# Revit family: Power-ModularDevices-GEWISS-90RCD-BDHP_4P
name_source: partatom
category: Apparecchi elettrici
revit_build: Autodesk Revit MEP 2016 (Build: 20150220_1215(x64)
units: mm (PartAtom-declared; Revit-internal decimal feet)

## family parameters
Condiviso = Sì
Host = Superficie
Mantenere orientamento annotazione = Sì
Numero OmniClass = 23.80.50.00
Punto di calcolo locali = Sì
Quota connettore circolare = Usa diametro
Taglio con vuoti quando caricato = No
Tipo di parte = Normale
Titolo OmniClass = Terminals for Power Supply

## types (1)
- Power-ModularDevices-GEWISS-90RCD-BDHP_4P
    Adjustable tripping time = 0 - 60 - 150 ms
    Assembly position: = Any
    Catalogue = POWER
    Catalogue Range = 90 RCD
    Description = HIGH PERFORMANCE  RESIDUAL CURRENT DEVICE
    Descrizione = HP ADD-ON RCD 4P In<125A ADJ.A 0.3/3 6M
    EAN code = 8011564126121
    Electrocod = 1412
    IDF = 33a27205-77cd-423f-89ac-8c414bb87739
    IDT = fbd088cf-bf71-4337-bc4d-c5243847b385
    Idn = 300-3000MA
    Immagine tipo = GW95512.jpg
    Insulation voltage = 500V
    Label = BDHP
    Level of immunity (8/20 µs) = 3000A
    Modello = GW95512
    No. Chorus modules = 6
    No. modules = 6
    No. of modules EN 50022 = 6
    No. of poles = 4P
    Number of poles = 4P
    Numero di poli_ = 1
    Operating temperature = -25 +40 °C
    Overvoltage category = III
    Produttore = GEWISS S.p.A.
    Prospetto di default = 1219 mm
    Rated current (In) = 125A
    Rated current: = 125A
    Rated frequency (Hz) = 50Hz
    Rated impulse withstand voltage = 4KV
    Rated insulation voltage (Ui) = 500V
    Rated residual operating current = 300 - 3000 mA
    Rated tightening torque = 3.5 / 3 (terminals)
    Rated voltage = 400V
    Rated voltage (IEC/EN 60947-2 app. B) = 400V
    SEO = Add-on RCD
    Section flexible cable = Max 50 mm²
    Section rigid cable = Max 70 mm²
    Spostamento_x = -340 mm
    Standard = EN60947-2 dev. B
    Standard; = IEC/EN 60947-2 app. B
    Stocking temperature = -40 +70 °C
    Technical sheet = https://www.gewiss.com
    Time = 0 - 150ms
    Type = Adjustable
    Type: = Adjustable
    URL = https://www.gewiss.com
    Version file RFA = 19.0
    carico = Altro
    potenza in watt = 0 V
